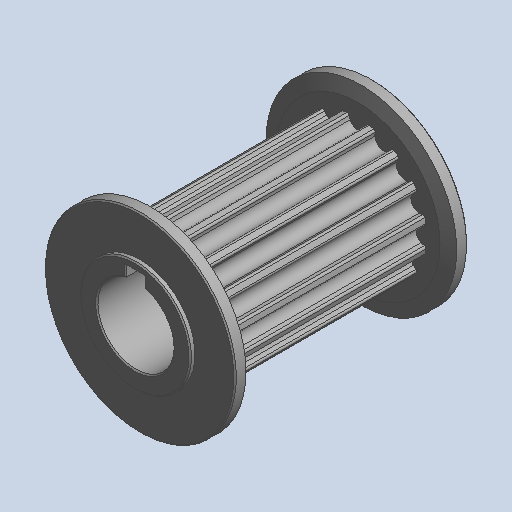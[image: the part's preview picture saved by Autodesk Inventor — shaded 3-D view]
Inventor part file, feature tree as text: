
AUTODESK INVENTOR PART (.ipt)
format: ipt  version: 2022.3 (Build 263350000, 350)  size: 248,832 bytes
history: native  units: mm (DEFAULTED — no unit token found)
features: chamfer x1
ambient origin geometry x8: Origin, YZ Plane, XZ Plane, XY Plane, X Axis, Y Axis, Z Axis, Center Point
bodies: Solid1 (feature_tree)
feature tree (1):
  chamfer  "Chamfer2"  [1 undecoded]
note: 1 required parameter value undecoded (feature->parameter linkage not recoverable at this tier; creation-order binding heuristic only, values carry confidence <= 0.55)
